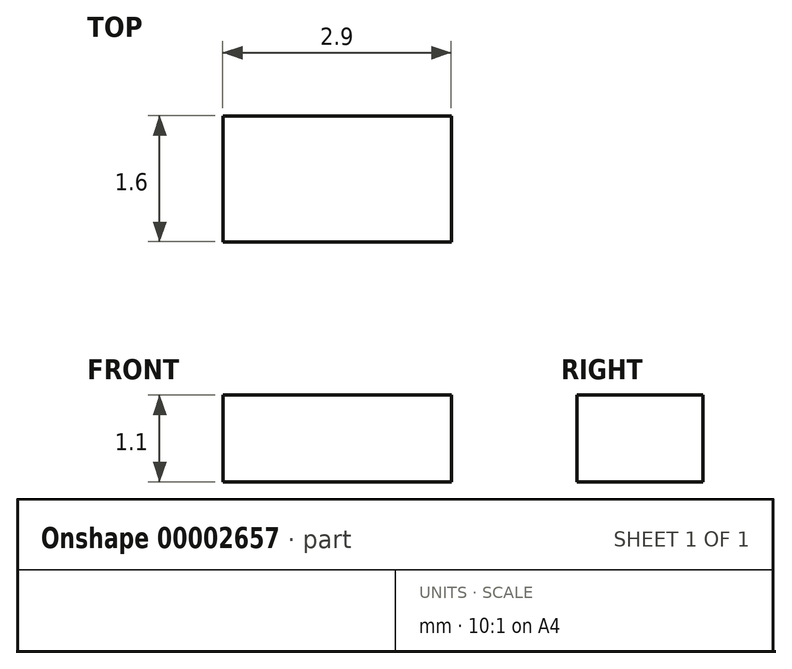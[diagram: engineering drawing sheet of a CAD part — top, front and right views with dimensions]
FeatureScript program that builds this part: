
annotation { "Feature Type Name" : "Feature", "Feature Type Description" : "" }
export const myFeature = defineFeature(function(context is Context, id is Id, definition is map)
    precondition{}
    {
        {
            var Q0;
            Q0=qCreatedBy(makeId("Top.planeOp"),FACE);
            var sketch = newSketch(context, id + "F0", { "sketchPlane" : qUnion([Q0])});
            skLineSegment(sketch, "E0.bottom", {"start": v(-4.39, 4.88) * mm, "end": v(-1.49, 4.88) * mm});
            skLineSegment(sketch, "E0.top", {"start": v(-4.39, 3.28) * mm, "end": v(-1.49, 3.28) * mm});
            skLineSegment(sketch, "E0.left", {"start": v(-4.39, 4.88) * mm, "end": v(-4.39, 3.28) * mm});
            skLineSegment(sketch, "E0.right", {"start": v(-1.49, 4.88) * mm, "end": v(-1.49, 3.28) * mm});
            skSolve(sketch);
        }
        {
            var Q0;
            Q0=makeQuery(id+"F0.imprint","IMPRINT",FACE,{"disambiguationData":[TD([[makeQuery(id+"F0.imprint","IMPRINT",EDGE,{"derivedFrom":sQuery(id+"F0.wireOp",EDGE,"E0.bottom")}),-1.0]])]});
            extrude(context, id + "F1", {"entities" : qUnion([Q0]), "depth" : 1.1 * mm});
        }
    });
